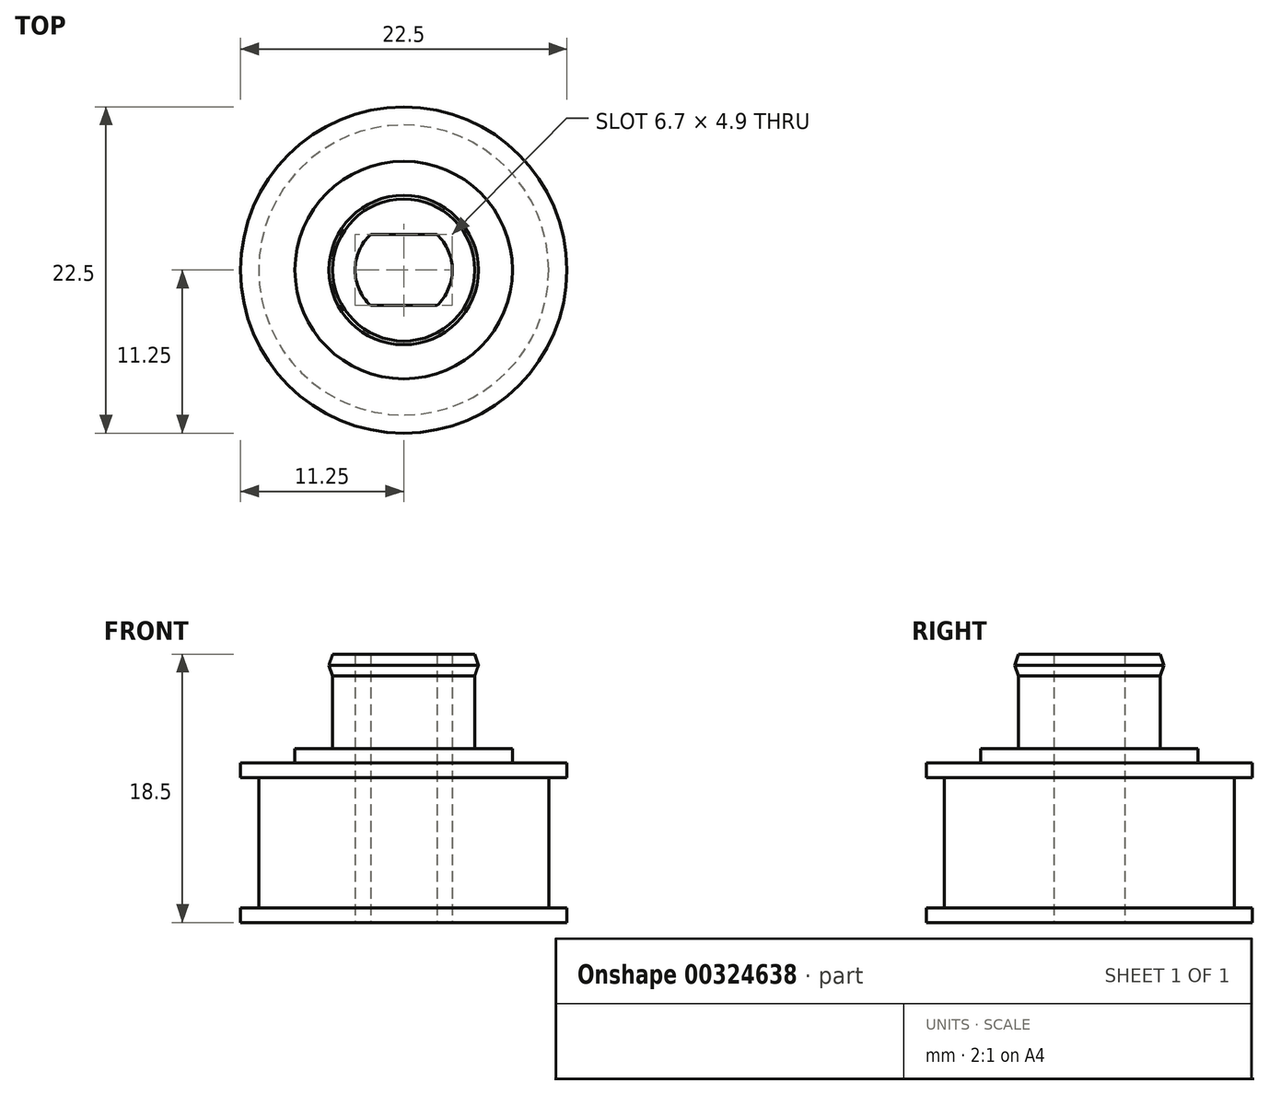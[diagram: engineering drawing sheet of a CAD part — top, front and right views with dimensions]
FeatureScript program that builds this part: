
annotation { "Feature Type Name" : "Feature", "Feature Type Description" : "" }
export const myFeature = defineFeature(function(context is Context, id is Id, definition is map)
    precondition{}
    {
        {
            assignVariable(context, id + "F0", {"name" : "e", "anyValue" : 6});
        }
        {
            assignVariable(context, id + "F1", {"name" : "h1", "anyValue" : 3});
        }
        {
            var Q0;
            Q0=qCreatedBy(makeId("Top.planeOp"),FACE);
            var sketch = newSketch(context, id + "F2", { "sketchPlane" : qUnion([Q0])});
            skCircle(sketch, "E0", {"center": v(0, 0) * mm, "radius": 10 * mm});
            skCircle(sketch, "E1", {"center": v(0, 0) * mm, "radius": 7.5 * mm});
            skCircle(sketch, "E2", {"center": v(0, 0) * mm, "radius": 4.9 * mm});
            skArc(sketch, "E3", {"start": v(-2.28, 2.45) * mm, "mid": v(-3.35, 0) * mm, "end": v(-2.28, -2.45) * mm});
            skLineSegment(sketch, "E4.bottom", {"start": v(2.28, -2.45) * mm, "end": v(-2.28, -2.45) * mm});
            skLineSegment(sketch, "E4.top", {"start": v(2.28, 2.45) * mm, "end": v(-2.28, 2.45) * mm});
            skArc(sketch, "E5.trimOffspring", {"start": v(2.28, -2.45) * mm, "mid": v(3.35, 0) * mm, "end": v(2.28, 2.45) * mm});
            skPoint(sketch, "E6.orphan", {"position": v(3.35, 2.45) * mm});
            skPoint(sketch, "E7.orphan", {"position": v(3.35, -2.45) * mm});
            skPoint(sketch, "E8.orphan", {"position": v(-3.35, -2.45) * mm});
            skPoint(sketch, "E9.orphan", {"position": v(-3.35, 2.45) * mm});
            skLineSegment(sketch, "E10", {"start": v(0, 7.5) * mm, "end": v(0, 10) * mm, "construction": true});
            skPoint(sketch, "E10.endSnap0", {"position": v(0, 2.45) * mm});
            skCircle(sketch, "E11", {"center": v(0, 0) * mm, "radius": 11.25 * mm});
            skSolve(sketch);
        }
        {
            var Q0;
            Q0=makeQuery(id+"F2.imprint","IMPRINT",FACE,{"disambiguationData":[TD([[makeQuery(id+"F2.imprint","IMPRINT",EDGE,{"derivedFrom":sQuery(id+"F2.wireOp",EDGE,"E0")}),1.0]])]});
            var Q1;
            Q1=makeQuery(id+"F2.imprint","IMPRINT",FACE,{"disambiguationData":[TD([[makeQuery(id+"F2.imprint","IMPRINT",EDGE,{"derivedFrom":sQuery(id+"F2.wireOp",EDGE,"E1")}),1.0]])]});
            var Q2;
            Q2=makeQuery(id+"F2.imprint","IMPRINT",FACE,{"disambiguationData":[TD([[makeQuery(id+"F2.imprint","IMPRINT",EDGE,{"derivedFrom":sQuery(id+"F2.wireOp",EDGE,"E2")}),1.0]])]});
            extrude(context, id + "F3", {"entities" : qUnion([Q0, Q1, Q2]), "depth" : 11 * mm});
        }
        {
            var Q0;
            Q0=makeQuery(id+"F2.imprint","IMPRINT",FACE,{"disambiguationData":[TD([[makeQuery(id+"F2.imprint","IMPRINT",EDGE,{"derivedFrom":sQuery(id+"F2.wireOp",EDGE,"E1")}),1.0]])]});
            var Q1;
            Q1=makeQuery(id+"F2.imprint","IMPRINT",FACE,{"disambiguationData":[TD([[makeQuery(id+"F2.imprint","IMPRINT",EDGE,{"derivedFrom":sQuery(id+"F2.wireOp",EDGE,"E2")}),1.0]])]});
            extrude(context, id + "F4", {"entities" : qUnion([Q0, Q1]), "operationType" : NewBodyOperationType.ADD, "depth" : (getVariable(context, 'e') + getVariable(context, 'h1')) * mm});
        }
        {
            var Q0;
            Q0=makeQuery(id+"F2.imprint","IMPRINT",FACE,{"disambiguationData":[TD([[makeQuery(id+"F2.imprint","IMPRINT",EDGE,{"derivedFrom":sQuery(id+"F2.wireOp",EDGE,"E2")}),1.0]])]});
            extrude(context, id + "F5", {"entities" : qUnion([Q0]), "operationType" : NewBodyOperationType.ADD, "depth" : 18.5 * mm});
        }
        {
            var Q0;
            Q0=qCreatedBy(makeId("Front.planeOp"),FACE);
            var sketch = newSketch(context, id + "F6", { "sketchPlane" : qUnion([Q0])});
            skLineSegment(sketch, "E12", {"start": v(0, 0) * mm, "end": v(0, 17.5) * mm, "construction": true});
            skLineSegment(sketch, "E13", {"start": v(-4.9, 6) * mm, "end": v(-4.9, 12.5) * mm});
            skLineSegment(sketch, "E14", {"start": v(4.9, 18.5) * mm, "end": v(4.9, 6) * mm});
            skLineSegment(sketch, "E15.bottom", {"start": v(4.9, 18.5) * mm, "end": v(5.15, 18.5) * mm, "construction": true});
            skLineSegment(sketch, "E15.top", {"start": v(4.9, 17) * mm, "end": v(5.15, 17) * mm, "construction": true});
            skLineSegment(sketch, "E15.left", {"start": v(4.9, 18.5) * mm, "end": v(4.9, 17) * mm, "construction": true});
            skLineSegment(sketch, "E15.right", {"start": v(5.15, 18.5) * mm, "end": v(5.15, 17) * mm, "construction": true});
            skPoint(sketch, "E16", {"position": v(5.15, 17.75) * mm});
            skLineSegment(sketch, "E17", {"start": v(4.9, 18.5) * mm, "end": v(5.15, 17.75) * mm});
            skLineSegment(sketch, "E18", {"start": v(5.15, 17.75) * mm, "end": v(4.9, 17) * mm});
            skLineSegment(sketch, "E19", {"start": v(4.9, 17) * mm, "end": v(4.9, 18.5) * mm});
            skSolve(sketch);
        }
        {
            var Q0;
            Q0=makeQuery(id+"F6.imprint","IMPRINT",FACE,{"disambiguationData":[TD([[makeQuery(id+"F6.imprint","IMPRINT",EDGE,{"derivedFrom":sQuery(id+"F6.wireOp",EDGE,"E17")}),-1.0]])]});
            var Q1;
            Q1=sQuery(id+"F6.wireOp",EDGE,"E12");
            revolve(context, id + "F7", {"operationType" : NewBodyOperationType.ADD, "entities" : qUnion([Q0]), "axis" : qUnion([Q1]), "revolveType" : RevolveType.FULL});
        }
        {
            var Q0;
            Q0=makeQuery(id+"F5.opExtrude","CAP_FACE",FACE,{"disambiguationData":[OSD([sQuery(id+"F2.wireOp",EDGE,"E2"),sQuery(id+"F2.wireOp",EDGE,"E3"),sQuery(id+"F2.wireOp",EDGE,"E4.bottom"),sQuery(id+"F2.wireOp",EDGE,"E4.top"),sQuery(id+"F2.wireOp",EDGE,"E5.trimOffspring")])],"isStart":false});
            cPlane(context, id + "F8", {"entities" : qUnion([Q0]), "cplaneType" : CPlaneType.OFFSET, "offset" : 0 * mm, "width" : 150 * mm, "height" : 150 * mm});
        }
        {
            var Q0;
            Q0=qCreatedBy(id+"F8.planeOp",FACE);
            var sketch = newSketch(context, id + "F9", { "sketchPlane" : qUnion([Q0])});
            skArc(sketch, "E20", {"start": v(-2.38, 2.7) * mm, "mid": v(-3.6, 0) * mm, "end": v(-2.38, -2.7) * mm});
            skLineSegment(sketch, "E21.bottom", {"start": v(-2.38, 2.7) * mm, "end": v(2.38, 2.7) * mm});
            skLineSegment(sketch, "E21.top", {"start": v(-2.38, -2.7) * mm, "end": v(2.38, -2.7) * mm});
            skPoint(sketch, "E22.orphan", {"position": v(4.18, 2.7) * mm});
            skPoint(sketch, "E23.orphan", {"position": v(3.52, -2.7) * mm});
            skArc(sketch, "E24.trimOffspring", {"start": v(2.38, -2.7) * mm, "mid": v(3.6, 0) * mm, "end": v(2.38, 2.7) * mm});
            skPoint(sketch, "E25.orphan", {"position": v(-4.18, -2.7) * mm});
            skPoint(sketch, "E26.orphan", {"position": v(-3.52, 2.7) * mm});
            skSolve(sketch);
        }
        {
            var Q0;
            Q0=qSketchRegion(id+"F2",true);
            extrude(context, id + "F10", {"entities" : qUnion([Q0]), "operationType" : NewBodyOperationType.ADD, "depth" : 1 * mm});
        }
        {
            var Q0;
            Q0=makeQuery(id+"F2.imprint","IMPRINT",FACE,{"disambiguationData":[TD([[makeQuery(id+"F2.imprint","IMPRINT",EDGE,{"derivedFrom":sQuery(id+"F2.wireOp",EDGE,"E0")}),1.0]])]});
            var Q1;
            Q1=makeQuery(id+"F10.opExtrude","CAP_FACE",FACE,{"disambiguationData":[OSD([sQuery(id+"F2.wireOp",EDGE,"E0"),sQuery(id+"F2.wireOp",EDGE,"E11")])],"isStart":false});
            extrude(context, id + "F11", {"entities" : qUnion([Q0, Q1]), "operationType" : NewBodyOperationType.ADD, "depth" : 10 * mm, "hasSecondDirection" : true, "secondDirectionOppositeDirection" : false, "secondDirectionDepth" : 9 * mm});
        }
        {
            var Q0;
            Q0=makeQuery(id+"F2.imprint","IMPRINT",FACE,{"disambiguationData":[TD([[makeQuery(id+"F2.imprint","IMPRINT",EDGE,{"derivedFrom":sQuery(id+"F2.wireOp",EDGE,"E1")}),1.0]])]});
            extrude(context, id + "F12", {"entities" : qUnion([Q0]), "operationType" : NewBodyOperationType.ADD, "depth" : 12 * mm});
        }
    });
